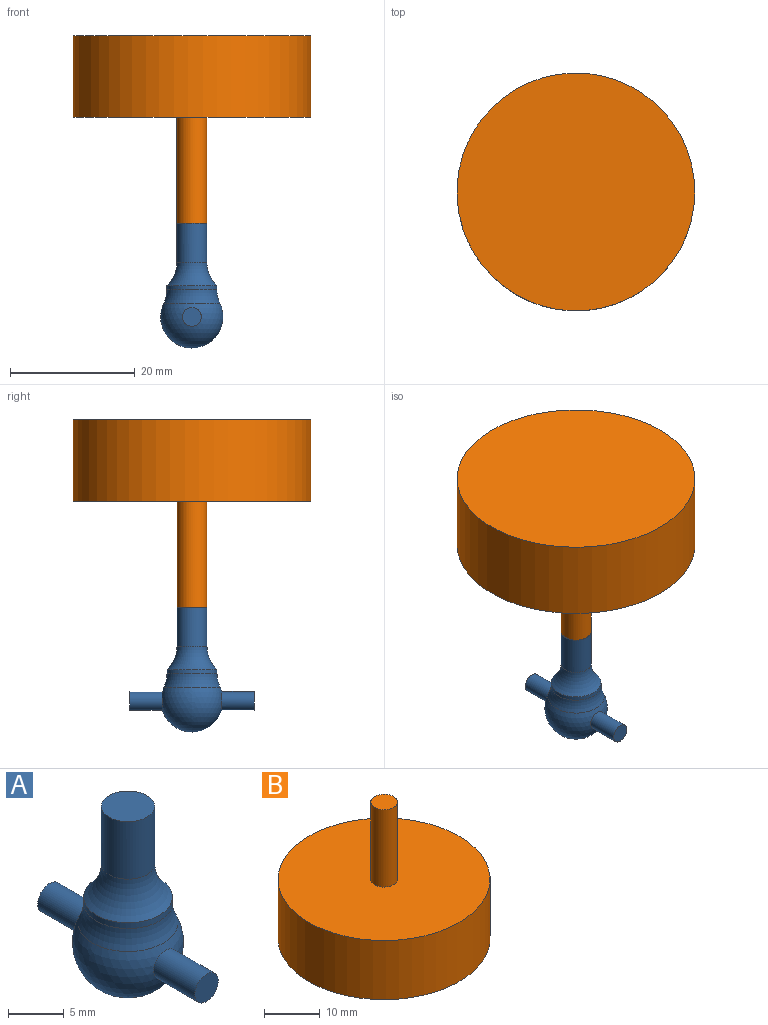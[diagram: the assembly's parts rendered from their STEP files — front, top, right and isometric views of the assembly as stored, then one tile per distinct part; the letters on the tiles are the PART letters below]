
ASSEMBLY  parts=2 mates=1
PART A: 10 faces, bbox 16x20x20 mm
  f0: sphere r=5mm, area 211.1mm2, adj f1,f3,f9
  f1: cylinder r=1.5mm len=5.23mm, axis (0,1,0), area 49.3mm2, adj f0,f2
  f2: plane 3x3mm, normal (0,-1,0), area 7.1mm2, adj f1
  f3: cylinder r=1.5mm len=5.23mm, axis (0,-1,0), area 49.3mm2, adj f0,f4
  f4: plane 3x3mm, normal (0,1,0), area 7.1mm2, adj f3
  f5: cylinder r=4mm len=8mm, axis (0,0,-1), area 16.1mm2, adj f8,f9
  f6: cylinder r=2.4mm len=6.33mm, axis (0,0,-1), area 95.5mm2, adj f7,f8
  f7: plane 4.8x4.8mm, normal (0,0,1), area 18.1mm2, adj f6
  f8: torus R=7.4mm, axis (0,0,-1), area 76.2mm2, adj f5,f6
  f9: torus R=9mm, axis (0,0,-1), area 59mm2, adj f0,f5
PART B: 5 faces, bbox 38.1x38.1x30 mm
  f0: cylinder r=19.05mm len=38.1mm, axis (0,0,-1), area 1556mm2, adj f1,f2
  f1: plane 38.1x38.1mm, normal (0,0,1), area 1122mm2, adj f0,f3
  f2: plane 38.1x38.1mm, normal (0,0,-1), area 1140.1mm2, adj f0
  f3: cylinder r=2.4mm len=17mm, axis (0,0,-1), area 256.4mm2, adj f1,f4
  f4: plane 4.8x4.8mm, normal (0,0,1), area 18.1mm2, adj f3
PLACE A t=(-2.12,1.97,-0.21)mm
PLACE B rot(axis=(1,0,0),180deg) t=(-2.12,1.97,44.79)mm
MATE fastened B.f3 <-> A.f6  axis (0,0,-1) through (-2.12,1.97,14.79)mm
